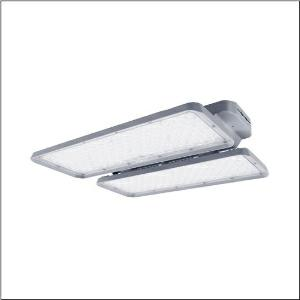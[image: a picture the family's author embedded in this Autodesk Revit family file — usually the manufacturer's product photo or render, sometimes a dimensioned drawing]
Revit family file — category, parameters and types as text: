
# Revit family: highbay_21-l_51hk41db4mca
name_source: partatom
category: Lighting Fixtures
units: mm (PartAtom-declared; Revit-internal decimal feet)

## family parameters
Cut with Voids When Loaded = No
Host = Face
Light Source = No
Part Type = Normal
Room Calculation Point = No
Round Connector Dimension = Use Diameter
Shared = No

## types (1)
- Highbay 21-L (1 x LED, 26200 lm, 147 W, 4000K)
    Apparent Load = 147 VA
    CIE Flux Codes = 87 97 99 100 100
    Color Rendering = 80
    Color Temperature = 4000K
    Default Elevation = 1800 mm
    Description = Highbay 21-L, LED high bay luminaire, primary light control with lens, of PC, light emission: direct distribution, primary light characteristic: symmetric, installation type: suspended mounting, surface-mounted, LED, rated luminous flux: 26.200lm, luminous efficacy: 180lm/W, light colour: 840, colour temperature: 4000K, with terminal, 5-pole, max. 2.5mm², mains connection: 220..240V, AC, 50Hz, rated input power: 147W, housing, of diecast aluminium, coated, grey, length: 471mm, width: 390mm, height: 87mm, protection rating (complete): IP66, insulation class (complete): insulation class I (protective earthing), certification: CE, ENEC, UKCA, protection symbol: D, impact resistance: IK08, permissible operating ambient temperature: -30..+60°C, corresponds to IFS (International Featured Standards) requirements for safety and quality in the food industry, LABS conformity tested according to VDMA 24364:2018-05, packaging unit: 1 piece
    Height = 89 mm
    Lamp = 1 x LED
    Lamp Light Flux = 26200 lm
    Lamp Power = 147 W
    Lamp count = 1
    Length = 471 mm
    Luminous efficacy = 178 lm/W
    Manufacturer = Siteco
    ModVariant = No
    Model = 51HK41DB4MCA
    Mounting Place = Ceiling
    Mounting Type = Pendant
    Number of Poles = 1
    OnlyDefault = Yes
    Power Factor = 1
    Product Name = Highbay 21-L
    Product group = LED high bay luminaire
    ProductGroupID = 903
    Protection Class = Protection class I
    Protection Degree = IP 66
    RLX_Detail_Level = 1
    RLX_Emergency_Light_Flux = 0 lm
    RLX_Emergency_Type = 0
    RLX_Emergency_Type_DB = No
    RlxData = <blob elided: 25425 chars, md5=6736a0eb>
    Socket = socket
    Standby Power = 0 W
    System Light Flux = 26200 lm
    System Power = 147 W
    Type Comments = Product without accessories
    Type Image = l_1276530.jpg
    URL = http://relux.com
    VarID = ---
    Voltage = 0 V
    Weight = 0.00 kg
    Width = 390 mm

## geometry (parser evidence)
native form markers: Blend x4, Sweep x12
no freeform markers — native parametric forms only
